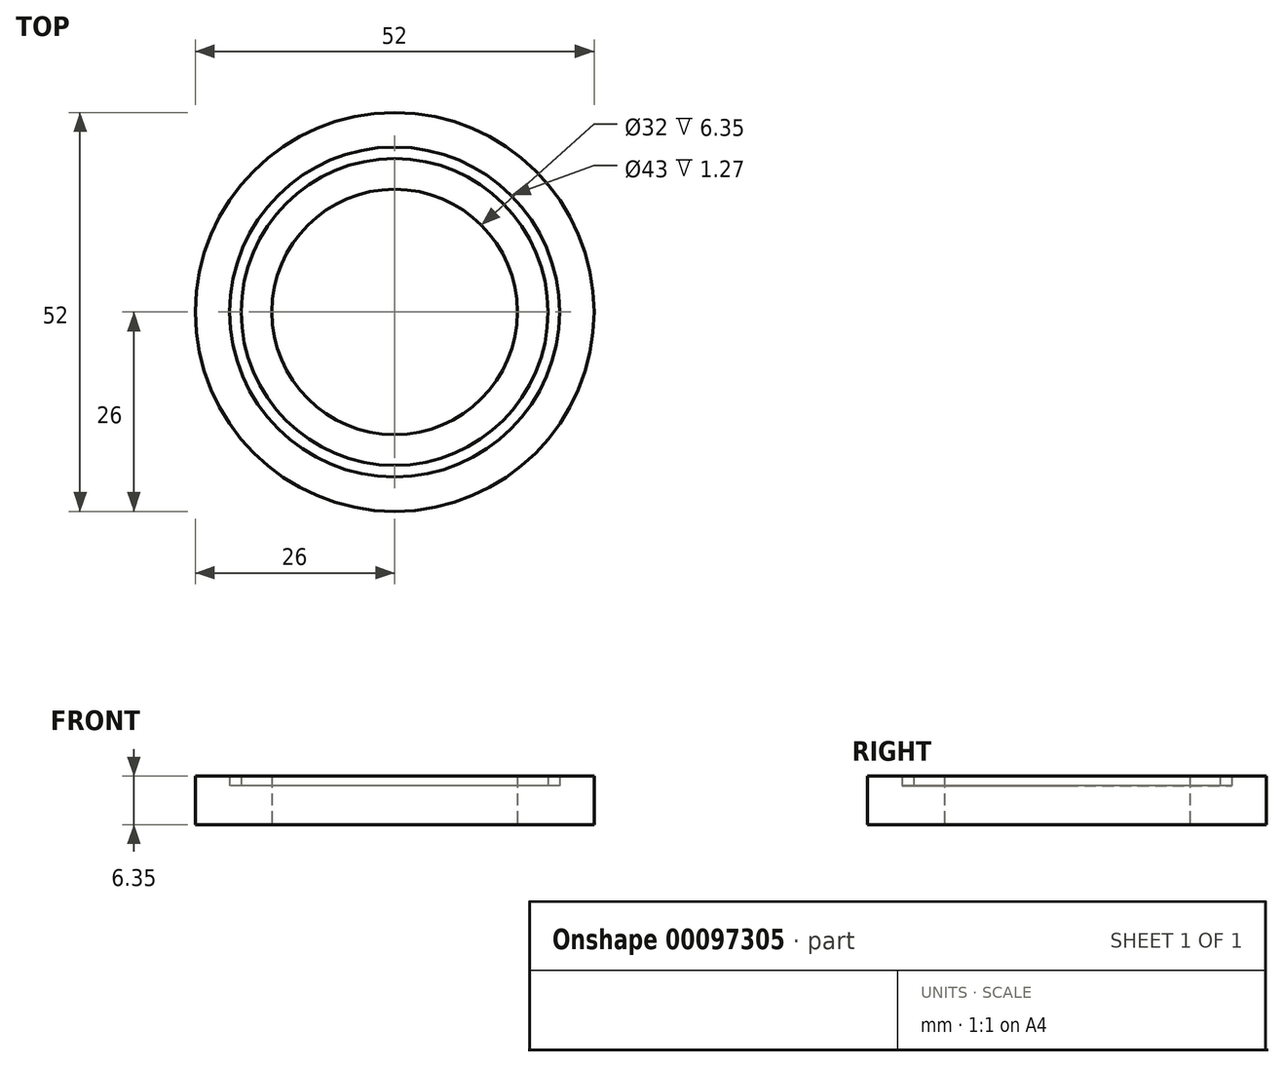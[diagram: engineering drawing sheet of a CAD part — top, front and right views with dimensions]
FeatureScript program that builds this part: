
annotation { "Feature Type Name" : "Feature", "Feature Type Description" : "" }
export const myFeature = defineFeature(function(context is Context, id is Id, definition is map)
    precondition{}
    {
        {
            var Q0;
            Q0=qCreatedBy(makeId("Top.planeOp"),FACE);
            var sketch = newSketch(context, id + "F0", { "sketchPlane" : qUnion([Q0])});
            skPoint(sketch, "E0", {"position": v(-16, 0) * mm});
            skPoint(sketch, "E1", {"position": v(-26, 0) * mm});
            skCircle(sketch, "E2", {"center": v(0, 0) * mm, "radius": 16 * mm});
            skCircle(sketch, "E3", {"center": v(0, 0) * mm, "radius": 26 * mm});
            skPoint(sketch, "E4", {"position": v(-21.5, 0) * mm});
            skPoint(sketch, "E5", {"position": v(-20, 0) * mm});
            skCircle(sketch, "E6", {"center": v(0, 0) * mm, "radius": 20 * mm});
            skCircle(sketch, "E7", {"center": v(0, 0) * mm, "radius": 21.5 * mm});
            skSolve(sketch);
        }
        {
            var Q0;
            Q0=makeQuery(id+"F0.imprint","IMPRINT",FACE,{"disambiguationData":[TD([[makeQuery(id+"F0.imprint","IMPRINT",EDGE,{"derivedFrom":sQuery(id+"F0.wireOp",EDGE,"E2")}),-1.0]])]});
            extrude(context, id + "F1", {"entities" : qUnion([Q0]), "depth" : 6.35 * mm});
        }
        {
            var Q0;
            Q0=makeQuery(id+"F0.imprint","IMPRINT",FACE,{"disambiguationData":[TD([[makeQuery(id+"F0.imprint","IMPRINT",EDGE,{"derivedFrom":sQuery(id+"F0.wireOp",EDGE,"E6")}),-1.0]])]});
            extrude(context, id + "F2", {"entities" : qUnion([Q0]), "operationType" : NewBodyOperationType.ADD, "depth" : 5.08 * mm});
        }
        {
            var Q0;
            Q0=makeQuery(id+"F0.imprint","IMPRINT",FACE,{"disambiguationData":[TD([[makeQuery(id+"F0.imprint","IMPRINT",EDGE,{"derivedFrom":sQuery(id+"F0.wireOp",EDGE,"E3")}),1.0]])]});
            extrude(context, id + "F3", {"entities" : qUnion([Q0]), "operationType" : NewBodyOperationType.ADD, "depth" : 6.35 * mm});
        }
    });
